# Revit family: SO12050
name_source: partatom
category: Aparatos eléctricos
revit_build: Autodesk Revit 2016 (Build: 20150220_1215(x64)
units: mm (PartAtom-declared; Revit-internal decimal feet)

## family parameters
Compartido = No
Corte con vacíos al cargar = No
Cota de conector redondo = Diámetro de uso
Mantener orientación de anotación = No
Número OmniClass = 23.80.00.00
Punto de cálculo de habitación = No
Se basa en plano de trabajo = No
Siempre vertical = Sí
Tipo de pieza = Caja de conexiones
Título OmniClass = Electric Power and Lighting

## types (1)
- Disipadores estáticos
    Coeficiente k = 5,96 W/m2
    Costo = 0 $
    Código de montaje = SO12050
    Descripción = DISIPADORES ESTÁTICOS
    Dimensiones = 2050 x 520 x 38mm
    Fabricante = SALVADOR ESCODA
    Imagen de tipo = disipador_estatico.png
    Material tubos/aletas = Cobre/aluminio
    Peso aprox. = 11,00 Kg
    Potencia disipación = 7334 W
    Presión máx = 10 bar
    Salto térmico = 65 ºC
    Superfície = 10,32 m2
    Temperatura exterior = 40 ºC
    Temperatura fluido = 105 ºC
    URL = www.salvadorescoda.com
